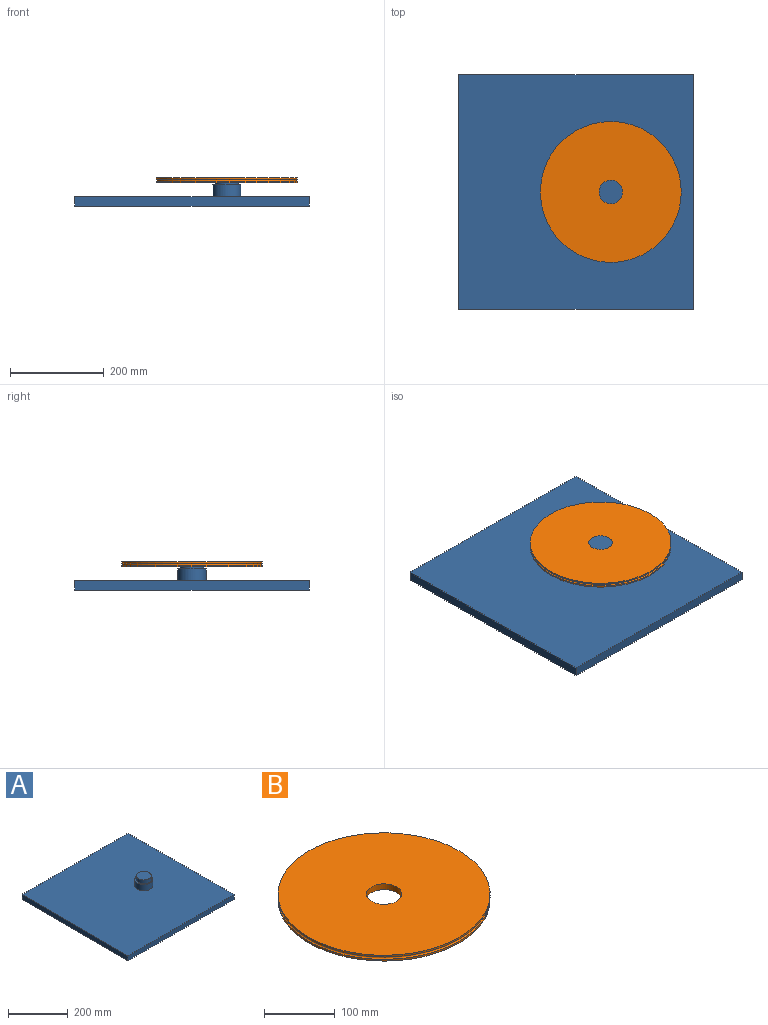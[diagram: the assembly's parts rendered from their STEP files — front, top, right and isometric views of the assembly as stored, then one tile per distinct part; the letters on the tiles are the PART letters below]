
ASSEMBLY  parts=2 mates=1
PART A: 10 faces, bbox 500x500x60 mm
  f0: plane 500x20mm, normal (0,-1,0), area 10000mm2, adj f1,f3,f4,f5
  f1: plane 500x20mm, normal (1,0,0), area 10000mm2, adj f0,f2,f4,f5
  f2: plane 500x20mm, normal (0,1,0), area 10000mm2, adj f1,f3,f4,f5
  f3: plane 500x20mm, normal (-1,0,0), area 10000mm2, adj f0,f2,f4,f5
  f4: plane 500x500mm, normal (0,0,1), area 247172.6mm2, adj f0,f1,f2,f3,f6
  f5: plane 500x500mm, normal (0,0,-1), area 250000mm2, adj f0,f1,f2,f3
  f6: cylinder r=30mm len=60mm, axis (0,0,-1), area 4712.4mm2, adj f4,f7
  f7: plane 60x60mm, normal (0,0,1), area 863.9mm2, adj f6,f8
  f8: cylinder r=25mm len=50mm, axis (0,0,-1), area 2356.2mm2, adj f7,f9
  f9: plane 50x50mm, normal (0,0,1), area 1963.5mm2, adj f8
PART B: 6 faces, bbox 327.8x327.8x10 mm
  f0: cylinder r=150mm len=300mm, axis (0,0,1), area 2827.4mm2, adj f1,f4
  f1: plane 300x300mm, normal (0,0,1), area 68722.3mm2, adj f0,f5
  f2: plane 300x300mm, normal (0,0,-1), area 68722.3mm2, adj f3,f5
  f3: cylinder r=150mm len=300mm, axis (0,0,1), area 2827.4mm2, adj f2,f4
  f4: torus R=150mm, axis (0,0,1), area 5871.5mm2, adj f0,f3
  f5: cylinder r=25mm len=50mm, axis (0,0,1), area 1570.8mm2, adj f1,f2
PLACE A t=(3.18,35.4,-28.25)mm
PLACE B t=(77.28,35.4,26.75)mm
MATE revolute B.f5 <-> A.f8  axis (0,0,1) through (77.28,35.4,31.75)mm
